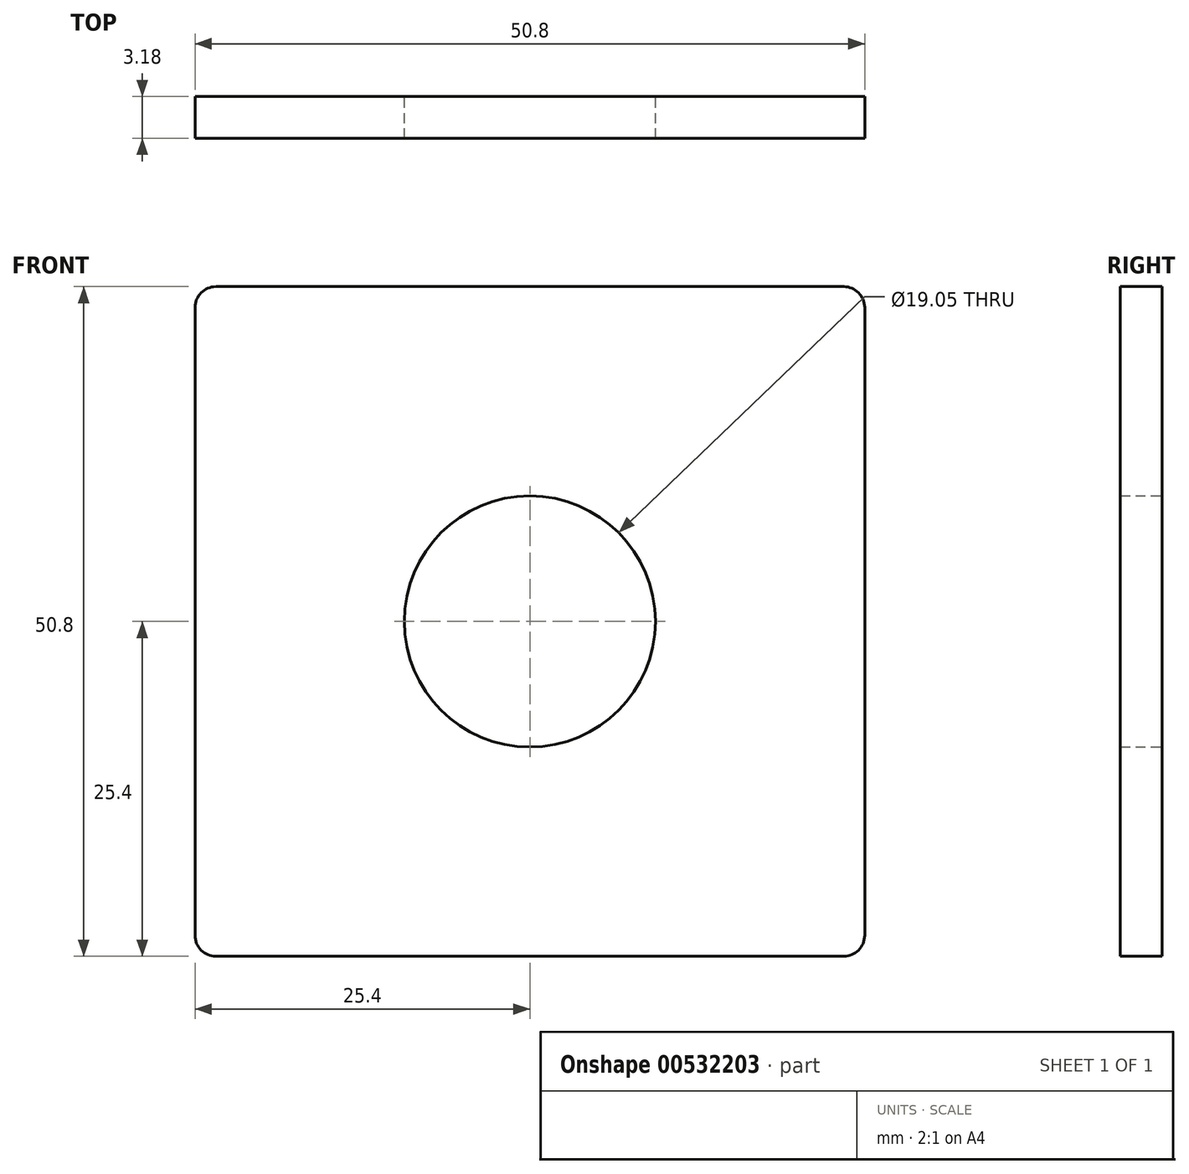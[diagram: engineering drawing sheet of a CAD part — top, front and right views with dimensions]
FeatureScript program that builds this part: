
annotation { "Feature Type Name" : "Feature", "Feature Type Description" : "" }
export const myFeature = defineFeature(function(context is Context, id is Id, definition is map)
    precondition{}
    {
        {
            var Q0;
            Q0=qCreatedBy(makeId("Front.planeOp"),FACE);
            var sketch = newSketch(context, id + "F0", { "sketchPlane" : qUnion([Q0])});
            skLineSegment(sketch, "E0.bottom", {"start": v(25.4, 25.4) * mm, "end": v(-25.4, 25.4) * mm});
            skLineSegment(sketch, "E0.top", {"start": v(25.4, -25.4) * mm, "end": v(-25.4, -25.4) * mm});
            skLineSegment(sketch, "E0.left", {"start": v(25.4, 25.4) * mm, "end": v(25.4, -25.4) * mm});
            skLineSegment(sketch, "E0.right", {"start": v(-25.4, 25.4) * mm, "end": v(-25.4, -25.4) * mm});
            skPoint(sketch, "E0.middle", {"position": v(0, 0) * mm});
            skSolve(sketch);
        }
        {
            var Q0;
            Q0 = qSketchRegion(id + "F0", true);
            extrude(context, id + "F1", {"entities" : qUnion([Q0]), "depth" : 3.17 * mm, "offsetDistance" : 25.4 * mm});
        }
        {
            var Q0;
            Q0=makeQuery(id+"F1.opExtrude","SWEPT_EDGE",EDGE,{"disambiguationData":[OSD([sQuery(id+"F0.wireOp",EDGE,"E0.bottom"),sQuery(id+"F0.wireOp",EDGE,"E0.left")])]});
            var Q1;
            Q1=makeQuery(id+"F1.opExtrude","SWEPT_EDGE",EDGE,{"disambiguationData":[OSD([sQuery(id+"F0.wireOp",EDGE,"E0.bottom"),sQuery(id+"F0.wireOp",EDGE,"E0.right")])]});
            var Q2;
            Q2=makeQuery(id+"F1.opExtrude","SWEPT_EDGE",EDGE,{"disambiguationData":[OSD([sQuery(id+"F0.wireOp",EDGE,"E0.top"),sQuery(id+"F0.wireOp",EDGE,"E0.right")])]});
            var Q3;
            Q3=makeQuery(id+"F1.opExtrude","SWEPT_EDGE",EDGE,{"disambiguationData":[OSD([sQuery(id+"F0.wireOp",EDGE,"E0.top"),sQuery(id+"F0.wireOp",EDGE,"E0.left")])]});
            fillet(context, id + "F2", {"entities" : qUnion([Q0, Q1, Q2, Q3]), "radius" : 1.59 * mm, "tangentPropagation" : true, "allowEdgeOverflow" : false});
        }
        {
            var Q0;
            Q0=makeQuery(id+"F1.opExtrude","CAP_FACE",FACE,{"disambiguationData":[OSD([sQuery(id+"F0.wireOp",EDGE,"E0.bottom"),sQuery(id+"F0.wireOp",EDGE,"E0.top"),sQuery(id+"F0.wireOp",EDGE,"E0.left"),sQuery(id+"F0.wireOp",EDGE,"E0.right")])],"isStart":true});
            var sketch = newSketch(context, id + "F3", { "sketchPlane" : qUnion([Q0])});
            skCircle(sketch, "E1", {"center": v(0, 0) * mm, "radius": 7.94 * mm, "construction": true});
            skCircle(sketch, "E2", {"center": v(0, 0) * mm, "radius": 13.34 * mm, "construction": true});
            skCircle(sketch, "E3", {"center": v(0, 0) * mm, "radius": 10.46 * mm, "construction": true});
            skCircle(sketch, "E4", {"center": v(0, 0) * mm, "radius": 9.53 * mm});
            skSolve(sketch);
        }
        {
            var Q0;
            Q0 = qSketchRegion(id + "F3", true);
            extrude(context, id + "F4", {"entities" : qUnion([Q0]), "operationType" : NewBodyOperationType.REMOVE, "endBound" : BoundingType.THROUGH_ALL, "oppositeDirection" : true, "depth" : 25.4 * mm, "offsetDistance" : 25.4 * mm});
        }
    });
